# Revit family: ТвінФреш Ізі
name_source: partatom
category: Mechanical Equipment
units: mm (PartAtom-declared; Revit-internal decimal feet)

## family parameters
Always vertical = Yes
Classification = None
Cut with Voids When Loaded = Yes
Part Type = Normal
Room Calculation Point = No
Round Connector Dimension = Use Diameter
Shared = No
Work Plane-Based = No

## types (2) — shared parameters
00_20_Виробник = Вентс
00_20_Назва = Провітрювач
B = 240 mm  [stored 0.787402 ft]
B1 = 186 mm  [stored 0.610236 ft]
D = 160 mm  [stored 0.524934 ft]
Dy = 155 mm  [stored 0.50853 ft]
L = 400 mm  [stored 1.31234 ft]
L2 = 86 mm  [stored 0.282152 ft]
Manufacturer = Вентс
URL = https://vents.ua
b = 180 mm  [stored 0.590551 ft]
b1 = 200 mm  [stored 0.656168 ft]
l1 = 200 mm  [stored 0.656168 ft]
l2 = 206 mm
l3 = 195 mm  [stored 0.639764 ft]
Вага = 5.00 kg
Висота = 250 mm  [stored 0.82021 ft]
Довжина = 532 mm  [stored 1.74541 ft]
Клас фільтрації = G3
Класифікація навантаження = HVAC
Колпак = No
Кількість фаз = 1
Максимальний потік повітря = 50.0 m³/h
Матеріал зони обслуговуваня = <By Category>
Матеріал корпусу = Метал, пофарбований, білий, матовий
Напруга = 230 V
Потужність = 4 W
Рівень звукового тиску на відстані 3 м = 29 дБА
Струм = 0.041 A
Частота = 50 Hz
Ширина = 250 mm  [stored 0.82021 ft]
zero-valued in all types: Default Elevation

## type names (no varying parameters)
- ТвінФреш Ізі РЛ7-50-17
- ТвінФреш Ізі-Д РЛ7-50-17

note: column(s) folded — value = type name in every type: 00_20_Тип

note: [stored X ft] marks values corroborated as IEEE doubles in the binary element streams (Revit-internal decimal feet)
